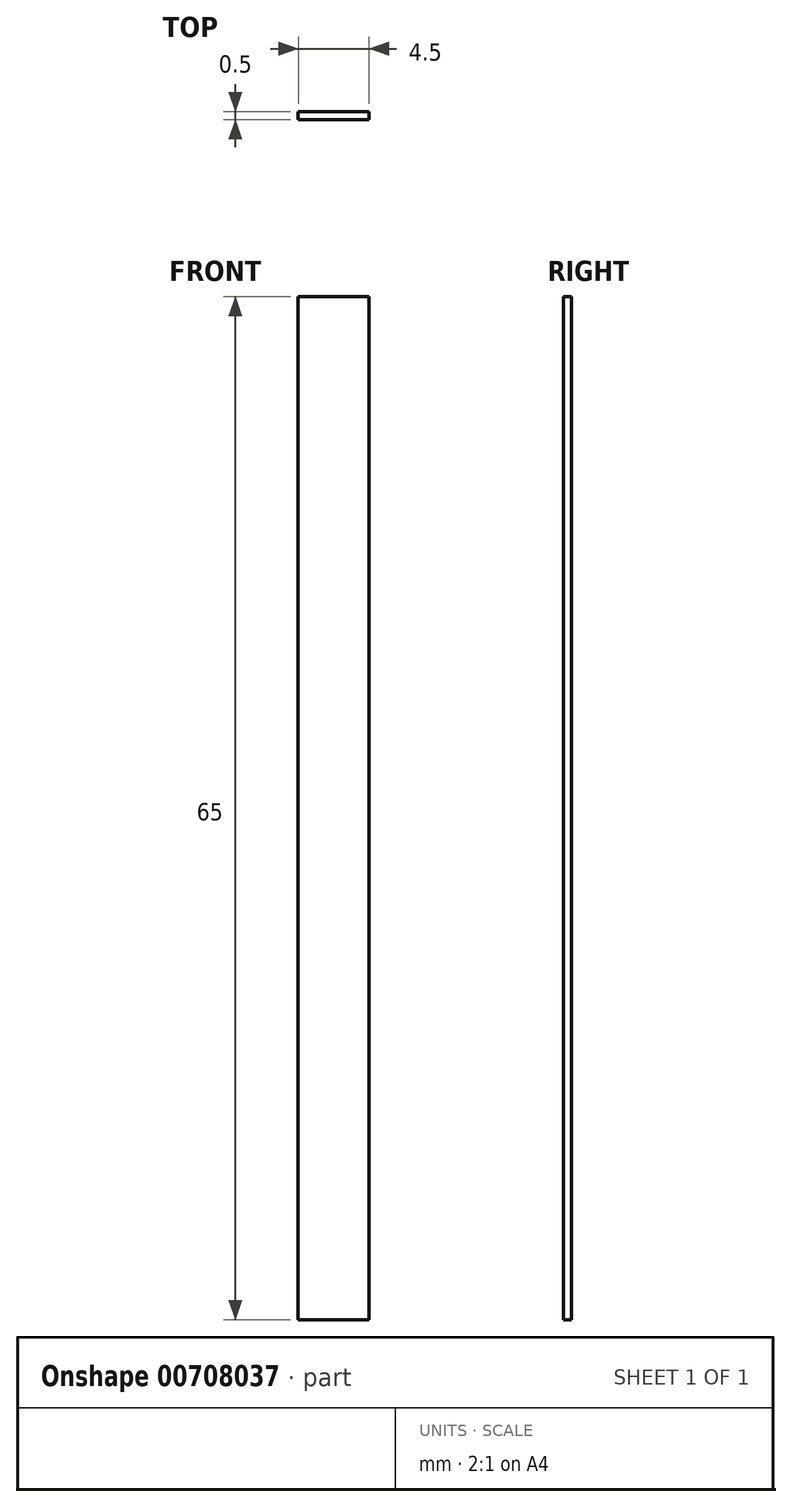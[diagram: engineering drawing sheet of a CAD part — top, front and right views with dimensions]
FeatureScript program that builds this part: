
annotation { "Feature Type Name" : "Feature", "Feature Type Description" : "" }
export const myFeature = defineFeature(function(context is Context, id is Id, definition is map)
    precondition{}
    {
        {
            var Q0;
            Q0=qCreatedBy(makeId("Front.planeOp"),FACE);
            var sketch = newSketch(context, id + "F0", { "sketchPlane" : qUnion([Q0])});
            skLineSegment(sketch, "E0.bottom", {"start": v(-2.36, 40.04) * mm, "end": v(2.14, 40.04) * mm});
            skLineSegment(sketch, "E0.top", {"start": v(-2.36, -24.96) * mm, "end": v(2.14, -24.96) * mm});
            skLineSegment(sketch, "E0.left", {"start": v(-2.36, 40.04) * mm, "end": v(-2.36, -24.96) * mm});
            skLineSegment(sketch, "E0.right", {"start": v(2.14, 40.04) * mm, "end": v(2.14, -24.96) * mm});
            skSolve(sketch);
        }
        {
            var Q0;
            Q0 = qSketchRegion(id + "F0", true);
            extrude(context, id + "F1", {"entities" : qUnion([Q0]), "depth" : 0.5 * mm, "offsetDistance" : 25 * mm});
        }
    });
